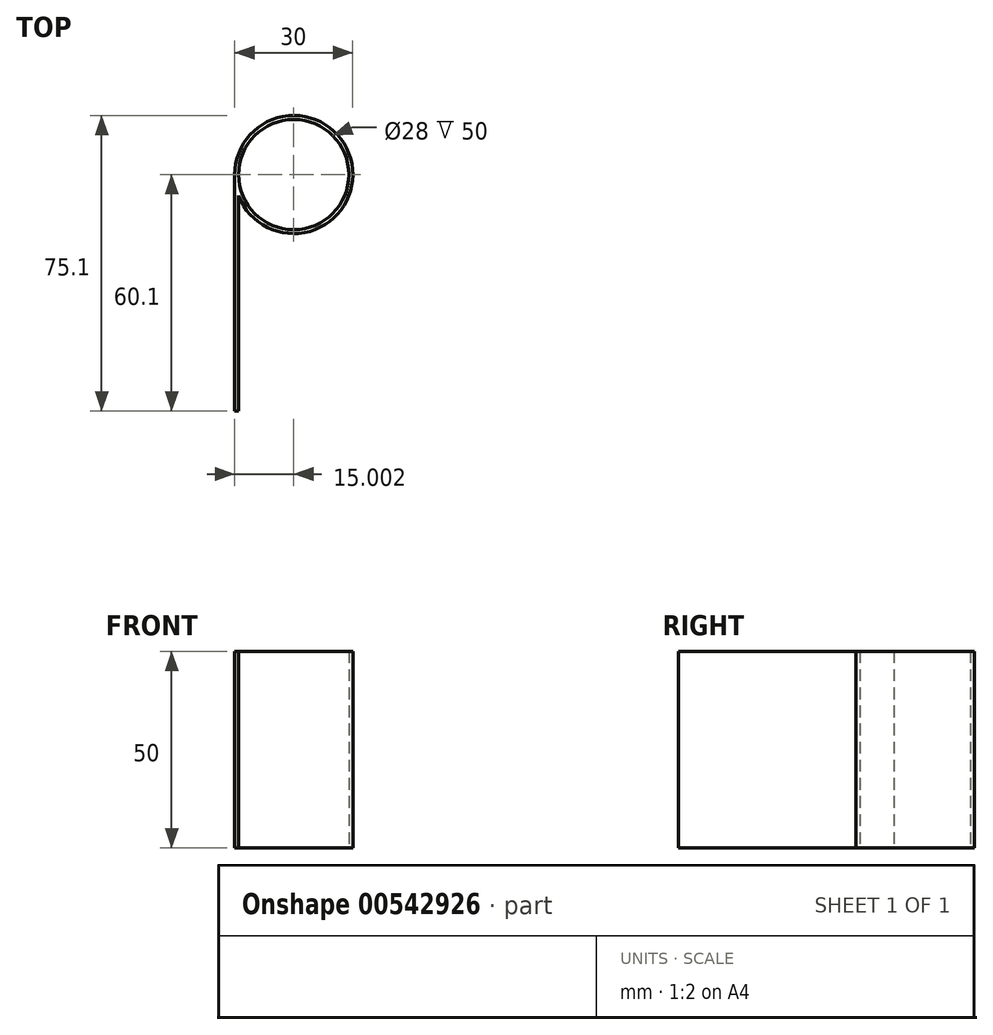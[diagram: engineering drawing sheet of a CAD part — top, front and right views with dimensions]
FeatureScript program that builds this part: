
annotation { "Feature Type Name" : "Feature", "Feature Type Description" : "" }
export const myFeature = defineFeature(function(context is Context, id is Id, definition is map)
    precondition{}
    {
        {
            var Q0;
            Q0=qCreatedBy(makeId("Top.planeOp"),FACE);
            var sketch = newSketch(context, id + "F0", { "sketchPlane" : qUnion([Q0])});
            skArc(sketch, "E0", {"start": v(-60.76, 44.84) * mm, "mid": v(-32, 52.97) * mm, "end": v(-61.76, 50.23) * mm});
            skLineSegment(sketch, "E1", {"start": v(-46.76, 50.23) * mm, "end": v(-31.76, 50.23) * mm, "construction": true});
            skLineSegment(sketch, "E2", {"start": v(-31.76, 50.23) * mm, "end": v(-46.76, 50.23) * mm, "construction": true});
            skLineSegment(sketch, "E3", {"start": v(-46.76, 50.23) * mm, "end": v(-61.76, 50.23) * mm, "construction": true});
            skLineSegment(sketch, "E4", {"start": v(-61.76, 50.23) * mm, "end": v(-61.76, 0) * mm});
            skLineSegment(sketch, "E5", {"start": v(-60.76, 0) * mm, "end": v(-60.76, 44.84) * mm});
            skCircle(sketch, "E6", {"center": v(-46.76, 50.23) * mm, "radius": 14 * mm});
            skLineSegment(sketch, "E7", {"start": v(-61.76, 0) * mm, "end": v(-61.76, -9.87) * mm});
            skLineSegment(sketch, "E8", {"start": v(-60.76, 0) * mm, "end": v(-60.76, -9.87) * mm});
            skLineSegment(sketch, "E9", {"start": v(-61.76, -9.87) * mm, "end": v(-60.76, -9.87) * mm});
            skSolve(sketch);
        }
        {
            var Q0;
            Q0=makeQuery(id+"F0.imprint","IMPRINT",FACE,{"disambiguationData":[TD([[makeQuery(id+"F0.imprint","IMPRINT",EDGE,{"derivedFrom":sQuery(id+"F0.wireOp",EDGE,"E0")}),1.0]])]});
            extrude(context, id + "F1", {"entities" : qUnion([Q0]), "depth" : 50 * mm, "offsetDistance" : 25 * mm});
        }
    });
